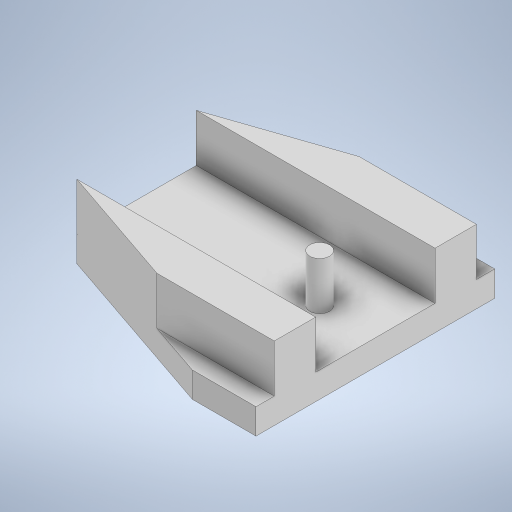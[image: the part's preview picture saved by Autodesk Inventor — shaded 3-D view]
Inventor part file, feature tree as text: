
AUTODESK INVENTOR PART (.ipt)
format: ipt  version: 2024.2 (Build 282272000, 272)  size: 275,968 bytes
history: native  units: mm
features: extrude x2, sketch x2
ambient origin geometry x8: Origin, YZ Plane, XZ Plane, XY Plane, X Axis, Y Axis, Z Axis, Center Point
bodies: Solid1 (feature_tree)
feature tree (4):
  extrude  "Extrusion1"  Depth=8.0mm
  extrude  "Extrusion2"  Depth=3.0mm
  sketch  "Sketch1"  dims[d0=30.0mm d1=8.0mm]
  sketch  "Sketch2"  dims[d2=4.5mm d3=3.0mm d4=3.0mm d5=17.2mm d6=3.4mm d7=1.75mm d8=15.0mm d10=7.5mm d11=22.0mm d12=22.0mm d13=3.2mm d14=0.0mm d17=2.5mm d21=1.1mm d22=1.1mm d23=15.0mm d24=7.0mm d25=6.0mm d26=0.0mm]
